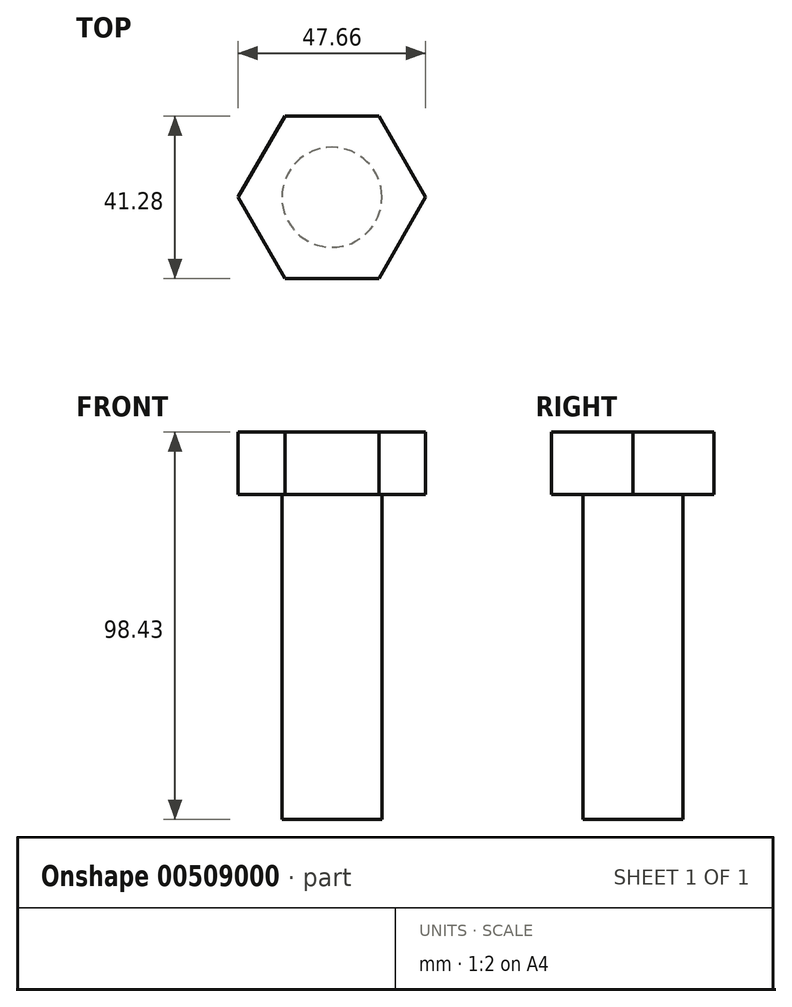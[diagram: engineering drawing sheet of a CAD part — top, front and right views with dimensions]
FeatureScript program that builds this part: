
annotation { "Feature Type Name" : "Feature", "Feature Type Description" : "" }
export const myFeature = defineFeature(function(context is Context, id is Id, definition is map)
    precondition{}
    {
        {
            var Q0;
            Q0=qCreatedBy(makeId("Top.planeOp"),FACE);
            var sketch = newSketch(context, id + "F0", { "sketchPlane" : qUnion([Q0])});
            skCircle(sketch, "E0", {"center": v(0, 0) * mm, "radius": 12.7 * mm});
            skSolve(sketch);
        }
        {
            var Q0;
            Q0=makeQuery(id+"F0.imprint","IMPRINT",FACE,{"disambiguationData":[TD([[makeQuery(id+"F0.imprint","IMPRINT",EDGE,{"derivedFrom":sQuery(id+"F0.wireOp",EDGE,"E0")}),1.0]])]});
            var Q1;
            Q1=qSketchRegion(id+"F2",true);
            extrude(context, id + "F1", {"entities" : qUnion([Q0, Q1]), "oppositeDirection" : true, "depth" : 82.55 * mm, "offsetDistance" : 25.4 * mm});
        }
        {
            var Q0;
            Q0=makeQuery(id+"F1.opExtrude","CAP_FACE",FACE,{"disambiguationData":[OSD([sQuery(id+"F0.wireOp",EDGE,"E0")])],"isStart":true});
            var sketch = newSketch(context, id + "F2", { "sketchPlane" : qUnion([Q0])});
            skCircle(sketch, "E1.cCircle", {"center": v(0, 0) * mm, "radius": 20.64 * mm, "construction": true});
            skLineSegment(sketch, "E1.0", {"start": v(-11.92, 20.64) * mm, "end": v(11.92, 20.64) * mm});
            skLineSegment(sketch, "E1.1", {"start": v(11.92, 20.64) * mm, "end": v(23.83, 0) * mm});
            skLineSegment(sketch, "E1.2", {"start": v(23.83, 0) * mm, "end": v(11.92, -20.64) * mm});
            skLineSegment(sketch, "E1.3", {"start": v(11.92, -20.64) * mm, "end": v(-11.92, -20.64) * mm});
            skLineSegment(sketch, "E1.4", {"start": v(-11.92, -20.64) * mm, "end": v(-23.83, 0) * mm});
            skLineSegment(sketch, "E1.5", {"start": v(-23.83, 0) * mm, "end": v(-11.92, 20.64) * mm});
            skPoint(sketch, "E1.0.midPoint", {"position": v(0, 20.64) * mm});
            skSolve(sketch);
        }
        {
            var Q0;
            Q0=qSketchRegion(id+"F2",true);
            extrude(context, id + "F3", {"entities" : qUnion([Q0]), "operationType" : NewBodyOperationType.ADD, "depth" : 15.88 * mm});
        }
    });
